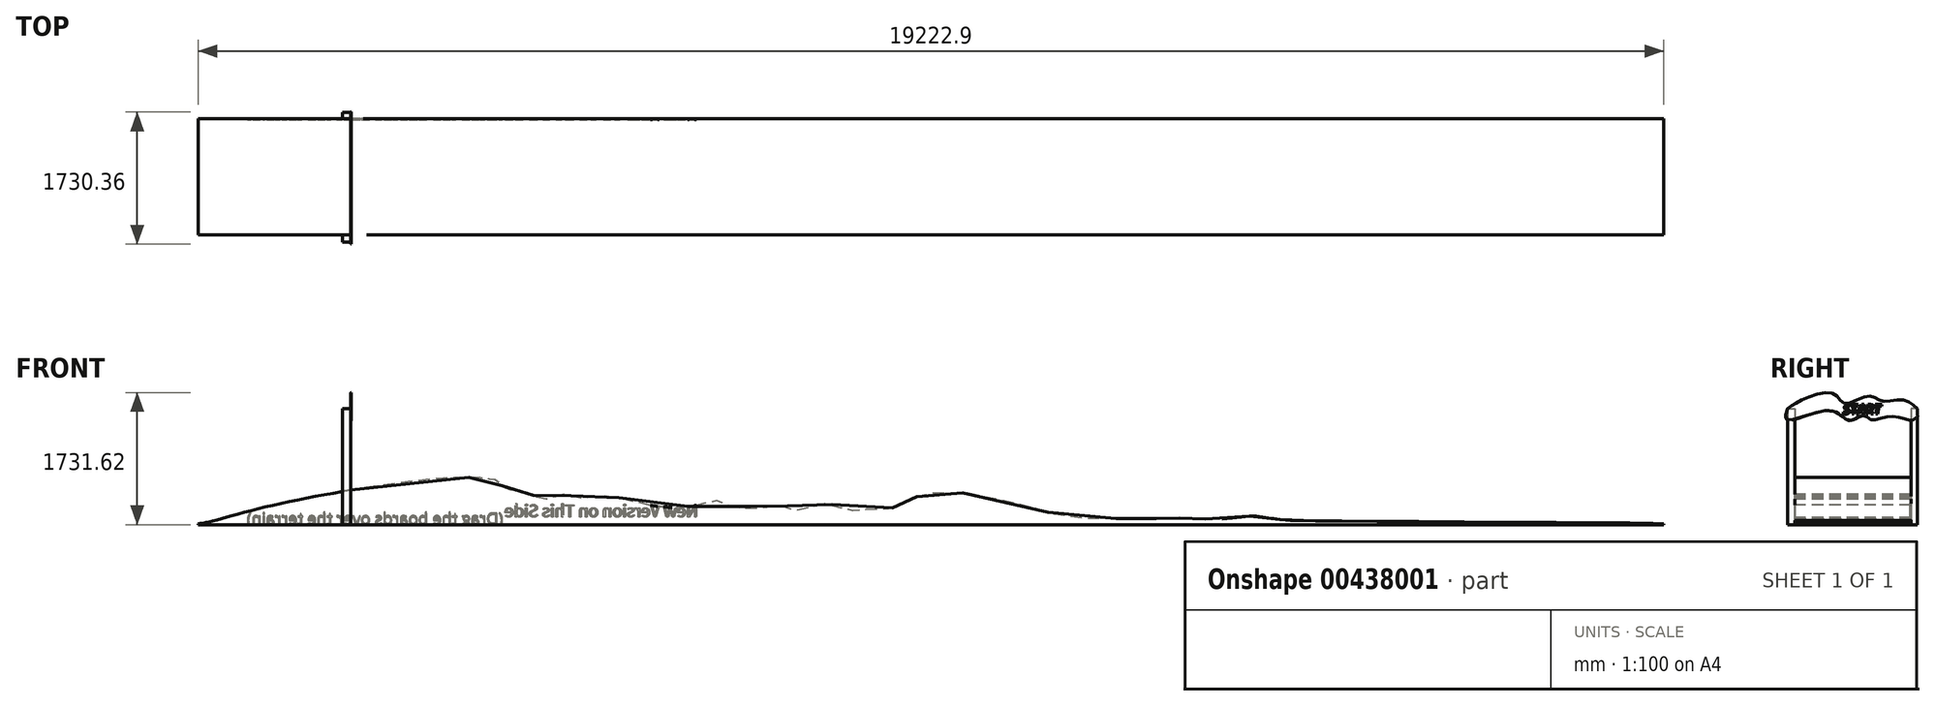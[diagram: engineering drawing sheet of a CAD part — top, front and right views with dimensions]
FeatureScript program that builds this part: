
annotation { "Feature Type Name" : "Feature", "Feature Type Description" : "" }
export const myFeature = defineFeature(function(context is Context, id is Id, definition is map)
    precondition{}
    {
        {
            var Q0;
            Q0=qCreatedBy(makeId("Top.planeOp"),FACE);
            var sketch = newSketch(context, id + "F0", { "sketchPlane" : qUnion([Q0])});
            skLineSegment(sketch, "E0.bottom", {"start": v(-12922.4, 1524) * mm, "end": v(6300.5, 1524) * mm});
            skLineSegment(sketch, "E0.top", {"start": v(-12922.4, 0) * mm, "end": v(6300.5, 0) * mm});
            skLineSegment(sketch, "E0.left", {"start": v(-12922.4, 1524) * mm, "end": v(-12922.4, 0) * mm});
            skLineSegment(sketch, "E0.right", {"start": v(6300.5, 1524) * mm, "end": v(6300.5, 0) * mm});
            skSolve(sketch);
        }
        {
            var Q0;
            Q0=makeQuery(id+"F0.imprint","IMPRINT",FACE,{"disambiguationData":[TD([[makeQuery(id+"F0.imprint","IMPRINT",EDGE,{"derivedFrom":sQuery(id+"F0.wireOp",EDGE,"E0.bottom")}),-1.0]])]});
            extrude(context, id + "F1", {"entities" : qUnion([Q0]), "depth" : 12.7 * mm});
        }
        {
            var Q0;
            Q0=makeQuery(id+"F1.opExtrude","SWEPT_FACE",FACE,{"disambiguationData":[OSD([sQuery(id+"F0.wireOp",EDGE,"E0.bottom")])]});
            var sketch = newSketch(context, id + "F2", { "sketchPlane" : qUnion([Q0])});
            skFitSpline(sketch, "E1", {"points": [v(-6300.5, 12.7) * mm, v(-1663.07, 51.88) * mm, v(-1426, 56.24) * mm, v(-1353.5, 58.24) * mm, v(-1210.03, 76.97) * mm, v(-1095.4, 87.5) * mm, v(-938.34, 113.26) * mm, v(-693.16, 90.3) * mm, v(-335.92, 70.29) * mm, v(-205.83, 85.3) * mm, v(-79.94, 74.82) * mm, v(-13.25, 90.98) * mm, v(118.45, 77.13) * mm, v(225.83, 85.03) * mm, v(273.2, 90.85) * mm, v(340.34, 80.64) * mm, v(393.08, 87.29) * mm, v(425.7, 87.83) * mm, v(467.98, 87.82) * mm, v(1392.82, 86.82) * mm, v(1857.72, 186.35) * mm, v(3070.1, 429.97) * mm, v(3414.75, 379.4) * mm, v(3499.96, 364.5) * mm, v(3555.6, 324.73) * mm, v(3662.76, 288.7) * mm, v(3686.29, 269.3) * mm, v(4220.15, 164.1) * mm, v(4697.67, 272.97) * mm, v(5136.03, 186.16) * mm, v(5205.48, 251.26) * mm, v(5485.46, 195.31) * mm, v(5665.54, 238.24) * mm, v(5778.38, 212.2) * mm, v(5877.46, 258.11) * mm, v(6015.19, 235.53) * mm, v(6110.88, 308.77) * mm, v(6237.8, 288.17) * mm, v(6880.8, 238.08) * mm, v(7574.68, 373.3) * mm, v(7943.4, 349.1) * mm, v(8119.18, 396.75) * mm, v(8375.8, 331.4) * mm, v(8616.13, 425.24) * mm, v(8822.77, 457.62) * mm, v(8909.38, 488.79) * mm, v(9008.37, 579.42) * mm, v(9068.81, 594.2) * mm, v(9475.42, 620.19) * mm, v(12044.16, 230.87) * mm, v(12922.4, 12.7) * mm], "startDerivative": vector(5545.27, 467) * mm, "endDerivative": vector(9016.67, 44.78) * mm});
            skSolve(sketch);
        }
        {
            var Q0;
            Q0=makeQuery(id+"F2.imprint","IMPRINT",FACE,{"disambiguationData":[TD([[makeQuery(id+"F2.imprint","IMPRINT",EDGE,{"derivedFrom":sQuery(id+"F2.wireOp",EDGE,"2191e21b-6fa2-4abd-85ac-a112500016c7")}),-1.0]])]});
            var Q1;
            {var subQ0=sQuery(id+"F2.wireOp",EDGE,"E1");var subQ1=sQuery(id+"F0.wireOp",EDGE,"E0.bottom");var subQ2=makeQuery(id+"F1.opExtrude","CAP_EDGE",EDGE,{"disambiguationData":[OSD([subQ1])],"isStart":false});var subQ4=makeQuery(id+"F2.imprint","INTERSECT",VERTEX,{"derivedFrom":[subQ2,subQ0]});Q1=makeQuery(id+"F2.imprint","IMPRINT",FACE,{"disambiguationData":[TD([[makeQuery(id+"F2.imprint","IMPRINT",EDGE,{"disambiguationData":[TD([[subQ4,1.0]])],"derivedFrom":subQ0}),-1.0]])]});}
            var Q2;
            Q2=makeQuery(id+"F1.opExtrude","SWEPT_FACE",FACE,{"disambiguationData":[OSD([sQuery(id+"F0.wireOp",EDGE,"E0.top")])]});
            extrude(context, id + "F3", {"entities" : qUnion([Q0, Q1]), "operationType" : NewBodyOperationType.ADD, "endBound" : BoundingType.UP_TO_SURFACE, "oppositeDirection" : true, "endBoundEntityFace" : qUnion([Q2]), "depth" : 63.5 * mm});
        }
        {
            var Q0;
            {var subQ0=sQuery(id+"F0.wireOp",EDGE,"E0.bottom");Q0=makeQuery(id+"F3.boolean.opBoolean","MERGE",FACE,{"derivedFrom":[makeQuery(id+"F1.opExtrude","SWEPT_FACE",FACE,{"disambiguationData":[OSD([subQ0])]}),makeQuery(id+"F3.opExtrude","CAP_FACE",FACE,{"disambiguationData":[OSD([subQ0,sQuery(id+"F2.wireOp",EDGE,"E1")])],"isStart":true})]});}
            var sketch = newSketch(context, id + "F4", { "sketchPlane" : qUnion([Q0])});
            skText(sketch, "E2", { "text": "New Version on This Side", "fontName": "NotoSansCJKjp-Regular.otf"});
            skText(sketch, "E3", { "text": "(Drag the boards over the terrain)", "fontName": "OpenSans-Regular.ttf"});
            const initialGuessF4  = {"E2": [6.36553, 0.10175, 1, 0, 0.15661], "E3": [8.92201, 0, 1, 0, 0.15434]};
            skSetInitialGuess(sketch, initialGuessF4);
            skSolve(sketch);
        }
        {
            var Q0;
            Q0=qSketchRegion(id+"F4",true);
            extrude(context, id + "F5", {"entities" : qUnion([Q0]), "operationType" : NewBodyOperationType.REMOVE, "oppositeDirection" : true, "depth" : 12.7 * mm});
        }
        {
            var Q0;
            Q0=makeQuery(id+"F1.opExtrude","CAP_FACE",FACE,{"disambiguationData":[OSD([sQuery(id+"F0.wireOp",EDGE,"E0.bottom"),sQuery(id+"F0.wireOp",EDGE,"E0.top"),sQuery(id+"F0.wireOp",EDGE,"E0.left"),sQuery(id+"F0.wireOp",EDGE,"E0.right")])],"isStart":true});
            var sketch = newSketch(context, id + "F6", { "sketchPlane" : qUnion([Q0])});
            skLineSegment(sketch, "E4.bottom", {"start": v(-11029.7, -1524) * mm, "end": v(-10920.6, -1524) * mm});
            skLineSegment(sketch, "E4.top", {"start": v(-11029.7, -1608.52) * mm, "end": v(-10920.6, -1608.52) * mm});
            skLineSegment(sketch, "E4.left", {"start": v(-11029.7, -1608.52) * mm, "end": v(-11029.7, -1524) * mm});
            skLineSegment(sketch, "E4.right", {"start": v(-10920.6, -1608.52) * mm, "end": v(-10920.6, -1524) * mm});
            skLineSegment(sketch, "E5.bottom", {"start": v(-11029.7, 0) * mm, "end": v(-10920.6, 0) * mm});
            skLineSegment(sketch, "E5.top", {"start": v(-11029.7, 95.33) * mm, "end": v(-10920.6, 95.33) * mm});
            skLineSegment(sketch, "E5.left", {"start": v(-11029.7, 95.33) * mm, "end": v(-11029.7, 0) * mm});
            skLineSegment(sketch, "E5.right", {"start": v(-10920.6, 95.33) * mm, "end": v(-10920.6, 0) * mm});
            skSolve(sketch);
        }
        {
            var Q0;
            Q0=qSketchRegion(id+"F6",true);
            extrude(context, id + "F7", {"entities" : qUnion([Q0]), "operationType" : NewBodyOperationType.ADD, "oppositeDirection" : true, "depth" : 1524 * mm});
        }
        {
            var Q0;
            Q0=makeQuery(id+"F7.opExtrude","SWEPT_FACE",FACE,{"disambiguationData":[OSD([sQuery(id+"F6.wireOp",EDGE,"E5.right")])]});
            var sketch = newSketch(context, id + "F8", { "sketchPlane" : qUnion([Q0])});
            skFitSpline(sketch, "E6", {"points": [v(-95.33, 1524) * mm, v(96.42, 1635.8) * mm, v(509.14, 1717.09) * mm, v(655.05, 1592.02) * mm, v(976.05, 1687.9) * mm, v(1136.56, 1623.29) * mm, v(1422.13, 1635.8) * mm, v(1605.56, 1524) * mm], "startDerivative": vector(1161.28, 794.44) * mm, "endDerivative": vector(1226.43, -1169.99) * mm});
            skFitSpline(sketch, "E7", {"points": [v(1605.56, 1524) * mm, v(1605.56, 1458.61) * mm, v(1597.22, 1406.5) * mm], "startDerivative": vector(30.72, -152.88) * mm, "endDerivative": vector(-152.11, -15.04) * mm});
            skFitSpline(sketch, "E8", {"points": [v(1597.22, 1406.5) * mm, v(1528.43, 1368.98) * mm, v(1376.27, 1406.5) * mm, v(1163.66, 1406.5) * mm, v(1007.32, 1373.15) * mm, v(896.85, 1431.52) * mm, v(719.67, 1364.81) * mm, v(475.79, 1496.13) * mm, v(-95.33, 1373.15) * mm, v(-95.33, 1524) * mm], "startDerivative": vector(-879.75, -750.95) * mm, "endDerivative": vector(628.47, 2102.15) * mm});
            skSolve(sketch);
        }
        {
            var Q0;
            Q0=qSketchRegion(id+"F8",true);
            extrude(context, id + "F9", {"entities" : qUnion([Q0]), "operationType" : NewBodyOperationType.ADD, "depth" : 2.54 * mm});
        }
        {
            var Q0;
            Q0=makeQuery(id+"F9.opExtrude","CAP_FACE",FACE,{"disambiguationData":[OSD([sQuery(id+"F8.wireOp",EDGE,"E6"),sQuery(id+"F8.wireOp",EDGE,"E7"),sQuery(id+"F8.wireOp",EDGE,"E8")])],"isStart":false});
            var sketch = newSketch(context, id + "F10", { "sketchPlane" : qUnion([Q0])});
            skText(sketch, "E9", { "text": "START", "fontName": "OpenSans-BoldItalic.ttf"});
            const initialGuessF10  = {"E9": [0.63299, 1.45046, 1, 0, 0.127]};
            skSetInitialGuess(sketch, initialGuessF10);
            skSolve(sketch);
        }
        {
            var Q0;
            Q0=qSketchRegion(id+"F10",true);
            extrude(context, id + "F11", {"entities" : qUnion([Q0]), "operationType" : NewBodyOperationType.REMOVE, "oppositeDirection" : true, "depth" : 1.27 * mm});
        }
        {
            var Q0;
            Q0=makeQuery(id+"F11.boolean.opBoolean","COPY",FACE,{"derivedFrom":makeQuery(id+"F11.opExtrude","CAP_FACE",FACE,{"disambiguationData":[OSD([sQuery(id+"F10.wireOp",EDGE,"E9.sketch_text.stroke-0"),sQuery(id+"F10.wireOp",EDGE,"E9.sketch_text.stroke-1"),sQuery(id+"F10.wireOp",EDGE,"E9.sketch_text.stroke-2"),sQuery(id+"F10.wireOp",EDGE,"E9.sketch_text.stroke-3"),sQuery(id+"F10.wireOp",EDGE,"E9.sketch_text.stroke-4"),sQuery(id+"F10.wireOp",EDGE,"E9.sketch_text.stroke-5"),sQuery(id+"F10.wireOp",EDGE,"E9.sketch_text.stroke-6"),sQuery(id+"F10.wireOp",EDGE,"E9.sketch_text.stroke-7"),sQuery(id+"F10.wireOp",EDGE,"E9.sketch_text.stroke-8"),sQuery(id+"F10.wireOp",EDGE,"E9.sketch_text.stroke-9"),sQuery(id+"F10.wireOp",EDGE,"E9.sketch_text.stroke-10"),sQuery(id+"F10.wireOp",EDGE,"E9.sketch_text.stroke-11"),sQuery(id+"F10.wireOp",EDGE,"E9.sketch_text.stroke-12"),sQuery(id+"F10.wireOp",EDGE,"E9.sketch_text.stroke-13"),sQuery(id+"F10.wireOp",EDGE,"E9.sketch_text.stroke-14"),sQuery(id+"F10.wireOp",EDGE,"E9.sketch_text.stroke-15"),sQuery(id+"F10.wireOp",EDGE,"E9.sketch_text.stroke-16"),sQuery(id+"F10.wireOp",EDGE,"E9.sketch_text.stroke-17"),sQuery(id+"F10.wireOp",EDGE,"E9.sketch_text.stroke-18"),sQuery(id+"F10.wireOp",EDGE,"E9.sketch_text.stroke-19"),sQuery(id+"F10.wireOp",EDGE,"E9.sketch_text.stroke-20"),sQuery(id+"F10.wireOp",EDGE,"E9.sketch_text.stroke-21"),sQuery(id+"F10.wireOp",EDGE,"E9.sketch_text.stroke-22"),sQuery(id+"F10.wireOp",EDGE,"E9.sketch_text.stroke-23")])],"isStart":false})});
            var Q1;
            Q1=makeQuery(id+"F11.boolean.opBoolean","COPY",FACE,{"derivedFrom":makeQuery(id+"F11.opExtrude","CAP_FACE",FACE,{"disambiguationData":[OSD([sQuery(id+"F10.wireOp",EDGE,"E9.sketch_text.stroke-24"),sQuery(id+"F10.wireOp",EDGE,"E9.sketch_text.stroke-25"),sQuery(id+"F10.wireOp",EDGE,"E9.sketch_text.stroke-26"),sQuery(id+"F10.wireOp",EDGE,"E9.sketch_text.stroke-27"),sQuery(id+"F10.wireOp",EDGE,"E9.sketch_text.stroke-28"),sQuery(id+"F10.wireOp",EDGE,"E9.sketch_text.stroke-29"),sQuery(id+"F10.wireOp",EDGE,"E9.sketch_text.stroke-30"),sQuery(id+"F10.wireOp",EDGE,"E9.sketch_text.stroke-31")])],"isStart":false})});
            var Q2;
            Q2=makeQuery(id+"F11.boolean.opBoolean","COPY",FACE,{"derivedFrom":makeQuery(id+"F11.opExtrude","CAP_FACE",FACE,{"disambiguationData":[OSD([sQuery(id+"F10.wireOp",EDGE,"E9.sketch_text.stroke-32"),sQuery(id+"F10.wireOp",EDGE,"E9.sketch_text.stroke-33"),sQuery(id+"F10.wireOp",EDGE,"E9.sketch_text.stroke-34"),sQuery(id+"F10.wireOp",EDGE,"E9.sketch_text.stroke-35"),sQuery(id+"F10.wireOp",EDGE,"E9.sketch_text.stroke-36"),sQuery(id+"F10.wireOp",EDGE,"E9.sketch_text.stroke-37"),sQuery(id+"F10.wireOp",EDGE,"E9.sketch_text.stroke-38"),sQuery(id+"F10.wireOp",EDGE,"E9.sketch_text.stroke-39"),sQuery(id+"F10.wireOp",EDGE,"E9.sketch_text.stroke-40"),sQuery(id+"F10.wireOp",EDGE,"E9.sketch_text.stroke-41"),sQuery(id+"F10.wireOp",EDGE,"E9.sketch_text.stroke-42"),sQuery(id+"F10.wireOp",EDGE,"E9.sketch_text.stroke-43"),sQuery(id+"F10.wireOp",EDGE,"E9.sketch_text.stroke-44"),sQuery(id+"F10.wireOp",EDGE,"E9.sketch_text.stroke-45")])],"isStart":false})});
            var Q3;
            Q3=makeQuery(id+"F11.boolean.opBoolean","COPY",FACE,{"derivedFrom":makeQuery(id+"F11.opExtrude","CAP_FACE",FACE,{"disambiguationData":[OSD([sQuery(id+"F10.wireOp",EDGE,"E9.sketch_text.stroke-65"),sQuery(id+"F10.wireOp",EDGE,"E9.sketch_text.stroke-66"),sQuery(id+"F10.wireOp",EDGE,"E9.sketch_text.stroke-67"),sQuery(id+"F10.wireOp",EDGE,"E9.sketch_text.stroke-68"),sQuery(id+"F10.wireOp",EDGE,"E9.sketch_text.stroke-69"),sQuery(id+"F10.wireOp",EDGE,"E9.sketch_text.stroke-70"),sQuery(id+"F10.wireOp",EDGE,"E9.sketch_text.stroke-71"),sQuery(id+"F10.wireOp",EDGE,"E9.sketch_text.stroke-72")])],"isStart":false})});
            var Q4;
            Q4=makeQuery(id+"F11.boolean.opBoolean","COPY",FACE,{"derivedFrom":makeQuery(id+"F11.opExtrude","CAP_FACE",FACE,{"disambiguationData":[OSD([sQuery(id+"F10.wireOp",EDGE,"E9.sketch_text.stroke-46"),sQuery(id+"F10.wireOp",EDGE,"E9.sketch_text.stroke-47"),sQuery(id+"F10.wireOp",EDGE,"E9.sketch_text.stroke-48"),sQuery(id+"F10.wireOp",EDGE,"E9.sketch_text.stroke-49"),sQuery(id+"F10.wireOp",EDGE,"E9.sketch_text.stroke-50"),sQuery(id+"F10.wireOp",EDGE,"E9.sketch_text.stroke-51"),sQuery(id+"F10.wireOp",EDGE,"E9.sketch_text.stroke-52"),sQuery(id+"F10.wireOp",EDGE,"E9.sketch_text.stroke-53"),sQuery(id+"F10.wireOp",EDGE,"E9.sketch_text.stroke-54"),sQuery(id+"F10.wireOp",EDGE,"E9.sketch_text.stroke-55"),sQuery(id+"F10.wireOp",EDGE,"E9.sketch_text.stroke-56"),sQuery(id+"F10.wireOp",EDGE,"E9.sketch_text.stroke-57"),sQuery(id+"F10.wireOp",EDGE,"E9.sketch_text.stroke-58"),sQuery(id+"F10.wireOp",EDGE,"E9.sketch_text.stroke-59"),sQuery(id+"F10.wireOp",EDGE,"E9.sketch_text.stroke-60"),sQuery(id+"F10.wireOp",EDGE,"E9.sketch_text.stroke-61"),sQuery(id+"F10.wireOp",EDGE,"E9.sketch_text.stroke-62"),sQuery(id+"F10.wireOp",EDGE,"E9.sketch_text.stroke-63"),sQuery(id+"F10.wireOp",EDGE,"E9.sketch_text.stroke-64")])],"isStart":false})});
            extrude(context, id + "F12", {"entities" : qUnion([Q0, Q1, Q2, Q3, Q4]), "depth" : 5.08 * mm});
        }
    });
